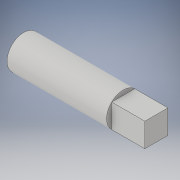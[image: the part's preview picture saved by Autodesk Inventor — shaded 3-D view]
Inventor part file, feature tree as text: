
AUTODESK INVENTOR PART (.ipt)
format: ipt  version: 2019 (Build 230136000, 136)  size: 106,496 bytes
history: native  units: in
note: dims shown in document units (in); Inventor stores cm internally (conversion verified against a paired STEP export)
features: other x3, extrude x1, sketch x1
ambient origin geometry x8: Origin, YZ Plane, XZ Plane, XY Plane, X Axis, Y Axis, Z Axis, Center Point
bodies: Solid1 (feature_tree)
feature tree (5):
  other  "SkeletalStuff.ipt"
  extrude  "Extrusion1"  Depth=0.5in TaperAngle=0.0deg
  other  "Solid2::SkeletalStuff.ipt"
  other  "TaggingFeature1"
  sketch  "Sketch1"  dims[d0=0.3937in d1=0.5in d2=0.0in]
